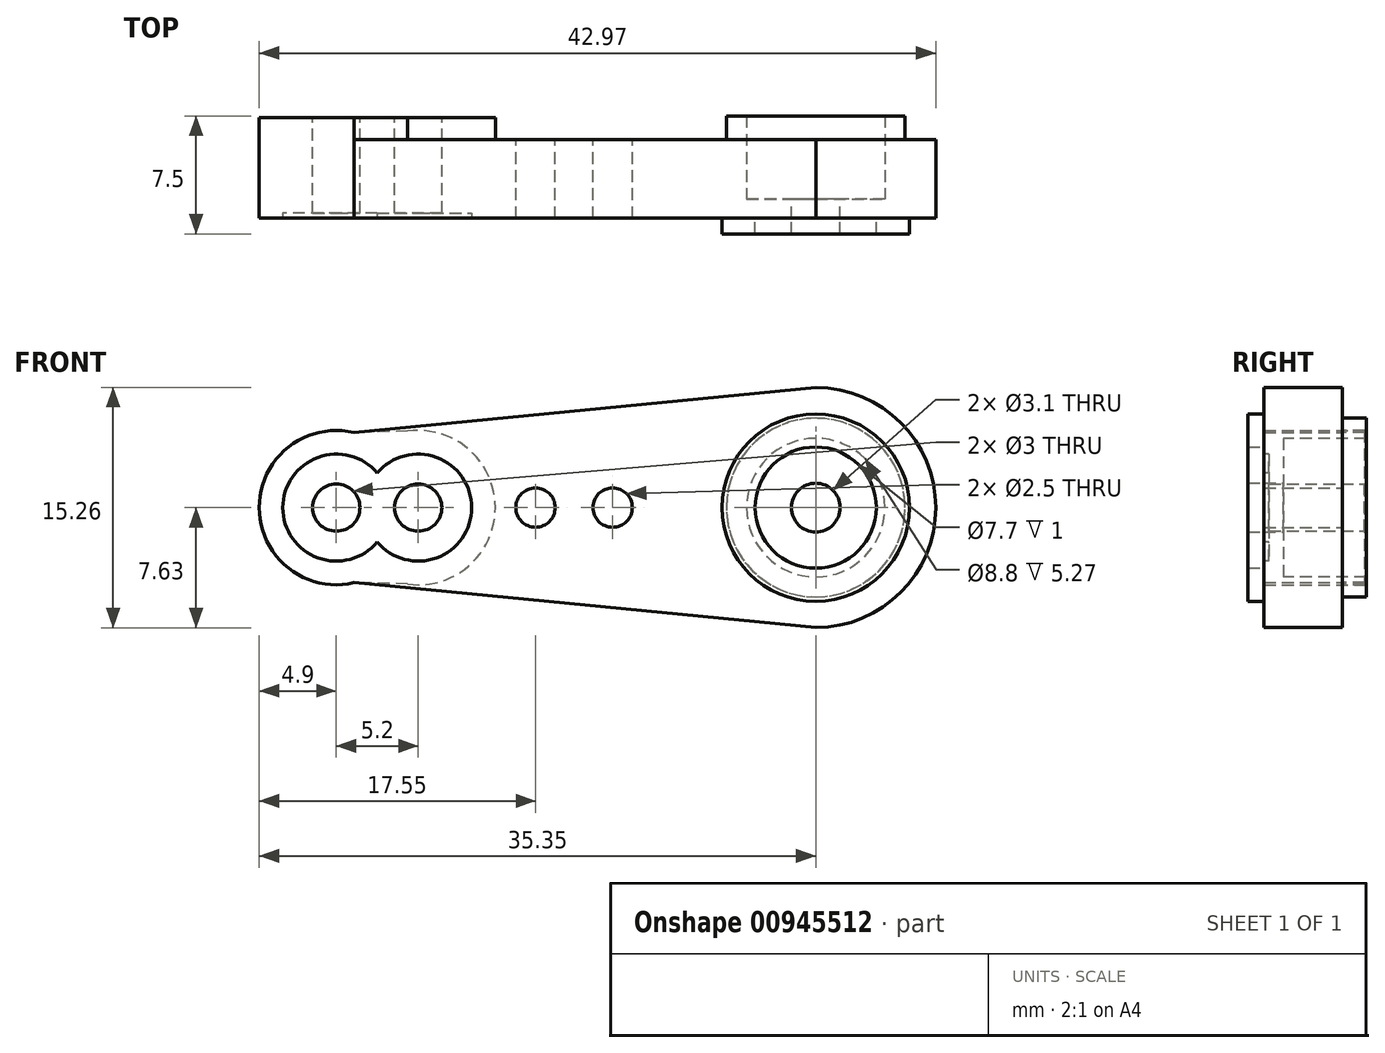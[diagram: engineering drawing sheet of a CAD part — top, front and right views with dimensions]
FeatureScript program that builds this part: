
annotation { "Feature Type Name" : "Feature", "Feature Type Description" : "" }
export const myFeature = defineFeature(function(context is Context, id is Id, definition is map)
    precondition{}
    {
        {
            var Q0;
            Q0=qCreatedBy(makeId("Front.planeOp"),FACE);
            var sketch = newSketch(context, id + "F0", { "sketchPlane" : qUnion([Q0])});
            skArc(sketch, "E0", {"start": v(-1.47, -7.48) * mm, "mid": v(7.62, 0) * mm, "end": v(-1.47, 7.48) * mm});
            skCircle(sketch, "E1", {"center": v(0, 0) * mm, "radius": 1.55 * mm});
            skCircle(sketch, "E2", {"center": v(-12.9, 0) * mm, "radius": 1.25 * mm});
            skCircle(sketch, "E3", {"center": v(-17.8, 0) * mm, "radius": 1.25 * mm});
            skCircle(sketch, "E4", {"center": v(-25.25, 0) * mm, "radius": 1.5 * mm});
            skCircle(sketch, "E5", {"center": v(-30.45, 0) * mm, "radius": 1.5 * mm});
            skArc(sketch, "E6", {"start": v(-29.33, 4.77) * mm, "mid": v(-35.35, 0) * mm, "end": v(-29.33, -4.77) * mm});
            skLineSegment(sketch, "E7", {"start": v(0, 7.62) * mm, "end": v(-29.33, 4.77) * mm});
            skLineSegment(sketch, "E8.MirrorCS", {"start": v(0, -7.63) * mm, "end": v(-29.33, -4.77) * mm});
            skSolve(sketch);
        }
        {
            var Q0;
            Q0=makeQuery(id+"F0.imprint","IMPRINT",FACE,{"disambiguationData":[TD([[makeQuery(id+"F0.imprint","IMPRINT",EDGE,{"derivedFrom":sQuery(id+"F0.wireOp",EDGE,"E1")}),-1.0]])]});
            extrude(context, id + "F1", {"entities" : qUnion([Q0]), "depth" : 5 * mm, "offsetDistance" : 25 * mm});
        }
        {
            var Q0;
            Q0=makeQuery(id+"F1.opExtrude","CAP_FACE",FACE,{"disambiguationData":[OSD([sQuery(id+"F0.wireOp",EDGE,"E0"),sQuery(id+"F0.wireOp",EDGE,"E1"),sQuery(id+"F0.wireOp",EDGE,"E2"),sQuery(id+"F0.wireOp",EDGE,"E3"),sQuery(id+"F0.wireOp",EDGE,"E4"),sQuery(id+"F0.wireOp",EDGE,"E5"),sQuery(id+"F0.wireOp",EDGE,"E6"),sQuery(id+"F0.wireOp",EDGE,"E7"),sQuery(id+"F0.wireOp",EDGE,"E8.MirrorCS")])],"isStart":false});
            var sketch = newSketch(context, id + "F2", { "sketchPlane" : qUnion([Q0])});
            skCircle(sketch, "E9", {"center": v(-30.45, 0) * mm, "radius": 3.4 * mm});
            skCircle(sketch, "E10", {"center": v(-25.25, 0) * mm, "radius": 3.4 * mm});
            skCircle(sketch, "E11", {"center": v(0, 0) * mm, "radius": 3.85 * mm});
            skCircle(sketch, "E12", {"center": v(0, 0) * mm, "radius": 5.95 * mm});
            skSolve(sketch);
        }
        {
            var Q0;
            Q0=makeQuery(id+"F2.imprint","IMPRINT",FACE,{"disambiguationData":[TD([[makeQuery(id+"F2.imprint","IMPRINT",EDGE,{"derivedFrom":makeQuery(id+"F1.opExtrude","CAP_EDGE",EDGE,{"disambiguationData":[OSD([sQuery(id+"F0.wireOp",EDGE,"E5")])],"isStart":false})}),-1.0]])]});
            var Q1;
            {var subQ0=sQuery(id+"F2.wireOp",EDGE,"E10");var subQ1=sQuery(id+"F2.wireOp",EDGE,"E9");var subQ2=makeQuery(id+"F2.imprint","INTERSECT",VERTEX,{"disambiguationData":[OD(0.0)],"derivedFrom":[subQ1,subQ0]});Q1=makeQuery(id+"F2.imprint","IMPRINT",FACE,{"disambiguationData":[TD([[makeQuery(id+"F2.imprint","IMPRINT",EDGE,{"disambiguationData":[TD([[subQ2,-1.0]])],"derivedFrom":subQ1}),1.0]])]});}
            var Q2;
            Q2=makeQuery(id+"F2.imprint","IMPRINT",FACE,{"disambiguationData":[TD([[makeQuery(id+"F2.imprint","IMPRINT",EDGE,{"derivedFrom":makeQuery(id+"F1.opExtrude","CAP_EDGE",EDGE,{"disambiguationData":[OSD([sQuery(id+"F0.wireOp",EDGE,"E4")])],"isStart":false})}),-1.0]])]});
            extrude(context, id + "F3", {"entities" : qUnion([Q0, Q1, Q2]), "operationType" : NewBodyOperationType.REMOVE, "oppositeDirection" : true, "depth" : 0.33 * mm, "offsetDistance" : 25 * mm});
        }
        {
            var Q0;
            Q0=makeQuery(id+"F2.imprint","IMPRINT",FACE,{"disambiguationData":[TD([[makeQuery(id+"F2.imprint","IMPRINT",EDGE,{"derivedFrom":sQuery(id+"F2.wireOp",EDGE,"E11")}),-1.0]])]});
            extrude(context, id + "F4", {"entities" : qUnion([Q0]), "operationType" : NewBodyOperationType.ADD, "depth" : 1 * mm, "offsetDistance" : 25 * mm});
        }
        {
            var Q0;
            Q0=makeQuery(id+"F1.opExtrude","CAP_FACE",FACE,{"disambiguationData":[OSD([sQuery(id+"F0.wireOp",EDGE,"E0"),sQuery(id+"F0.wireOp",EDGE,"E1"),sQuery(id+"F0.wireOp",EDGE,"E2"),sQuery(id+"F0.wireOp",EDGE,"E3"),sQuery(id+"F0.wireOp",EDGE,"E4"),sQuery(id+"F0.wireOp",EDGE,"E5"),sQuery(id+"F0.wireOp",EDGE,"E6"),sQuery(id+"F0.wireOp",EDGE,"E7"),sQuery(id+"F0.wireOp",EDGE,"E8.MirrorCS")])],"isStart":true});
            var sketch = newSketch(context, id + "F5", { "sketchPlane" : qUnion([Q0])});
            skArc(sketch, "E13", {"start": v(27.85, -4.15) * mm, "mid": v(35.35, 0) * mm, "end": v(27.85, 4.15) * mm});
            skArc(sketch, "E14", {"start": v(27.85, 4.15) * mm, "mid": v(20.35, 0) * mm, "end": v(27.85, -4.15) * mm});
            skLineSegment(sketch, "E15", {"start": v(25.92, 4.85) * mm, "end": v(29.33, 4.77) * mm});
            skLineSegment(sketch, "E16.MirrorCS", {"start": v(25.92, -4.85) * mm, "end": v(29.33, -4.77) * mm});
            skCircle(sketch, "E17", {"center": v(25.25, 0) * mm, "radius": 1.5 * mm});
            skCircle(sketch, "E18", {"center": v(30.45, 0) * mm, "radius": 1.5 * mm});
            skCircle(sketch, "E19", {"center": v(0, 0) * mm, "radius": 4.4 * mm});
            skCircle(sketch, "E20", {"center": v(0, 0) * mm, "radius": 5.68 * mm});
            skSolve(sketch);
        }
        {
            var Q0;
            Q0=makeQuery(id+"F5.imprint","IMPRINT",FACE,{"disambiguationData":[TD([[makeQuery(id+"F5.imprint","IMPRINT",EDGE,{"derivedFrom":sQuery(id+"F5.wireOp",EDGE,"E17")}),1.0]])]});
            var Q1;
            {var subQ0=sQuery(id+"F5.wireOp",EDGE,"E15");Q1=makeQuery(id+"F5.imprint","IMPRINT",FACE,{"disambiguationData":[TD([[makeQuery(id+"F5.imprint","IMPRINT",EDGE,{"derivedFrom":subQ0}),-1.0]])]});}
            var Q2;
            {var subQ0=sQuery(id+"F5.wireOp",EDGE,"E16.MirrorCS");Q2=makeQuery(id+"F5.imprint","IMPRINT",FACE,{"disambiguationData":[TD([[makeQuery(id+"F5.imprint","IMPRINT",EDGE,{"derivedFrom":subQ0}),1.0]])]});}
            extrude(context, id + "F6", {"entities" : qUnion([Q0, Q1, Q2]), "operationType" : NewBodyOperationType.ADD, "depth" : 1.4 * mm, "offsetDistance" : 25 * mm});
        }
        {
            var Q0;
            Q0=makeQuery(id+"F5.imprint","IMPRINT",FACE,{"disambiguationData":[TD([[makeQuery(id+"F5.imprint","IMPRINT",EDGE,{"derivedFrom":sQuery(id+"F5.wireOp",EDGE,"E19")}),-1.0]])]});
            extrude(context, id + "F7", {"entities" : qUnion([Q0]), "operationType" : NewBodyOperationType.ADD, "depth" : 1.5 * mm, "offsetDistance" : 25 * mm});
        }
        {
            var Q0;
            Q0=makeQuery(id+"F5.imprint","IMPRINT",FACE,{"disambiguationData":[TD([[makeQuery(id+"F5.imprint","IMPRINT",EDGE,{"derivedFrom":sQuery(id+"F5.wireOp",EDGE,"E19")}),1.0]])]});
            extrude(context, id + "F8", {"entities" : qUnion([Q0]), "operationType" : NewBodyOperationType.REMOVE, "oppositeDirection" : true, "depth" : (4.1 - 0.33) * mm, "offsetDistance" : 25 * mm});
        }
        {
            var Q0;
            Q0=makeQuery(id+"F2.imprint","IMPRINT",FACE,{"disambiguationData":[TD([[makeQuery(id+"F2.imprint","IMPRINT",EDGE,{"derivedFrom":sQuery(id+"F2.wireOp",EDGE,"E11")}),1.0]])]});
            extrude(context, id + "F9", {"entities" : qUnion([Q0]), "depth" : 1 * mm, "offsetDistance" : 25 * mm});
        }
    });
